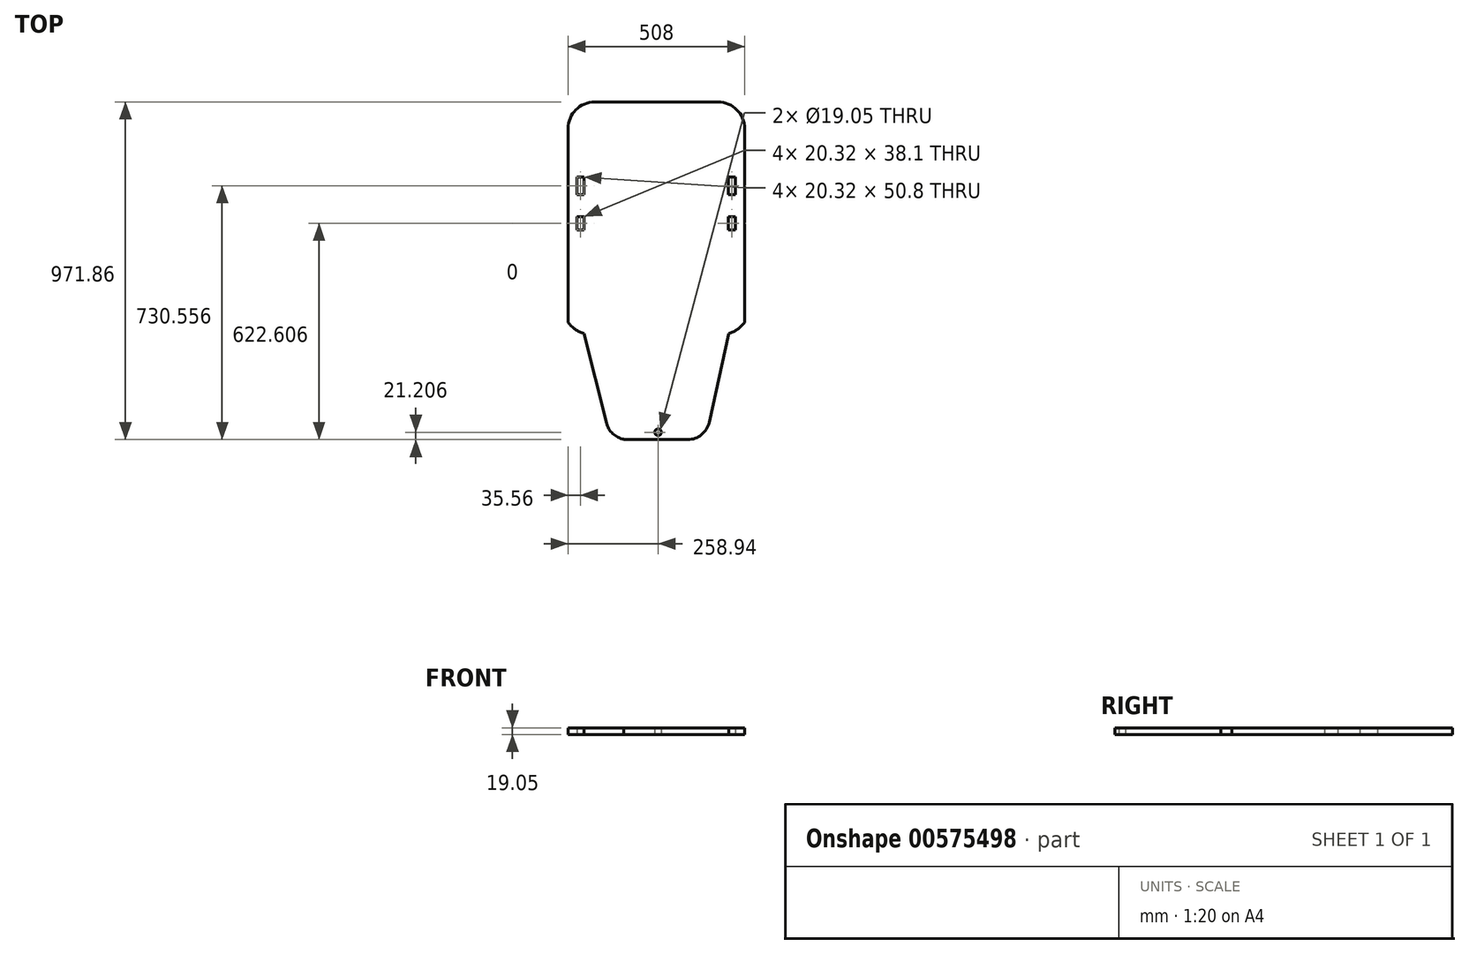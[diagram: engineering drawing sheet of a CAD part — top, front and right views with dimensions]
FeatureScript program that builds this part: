
annotation { "Feature Type Name" : "Feature", "Feature Type Description" : "" }
export const myFeature = defineFeature(function(context is Context, id is Id, definition is map)
    precondition{}
    {
        {
            var Q0;
            Q0=qCreatedBy(makeId("Top.planeOp"),FACE);
            var sketch = newSketch(context, id + "F0", { "sketchPlane" : qUnion([Q0])});
            skLineSegment(sketch, "E0.bottom", {"start": v(-318.66, 535.1) * mm, "end": v(189.34, 535.1) * mm});
            skLineSegment(sketch, "E0.left", {"start": v(-318.66, 535.1) * mm, "end": v(-318.66, 65.2) * mm});
            skLineSegment(sketch, "E0.right", {"start": v(189.34, 535.1) * mm, "end": v(189.34, 65.2) * mm});
            skLineSegment(sketch, "E1", {"start": v(87.68, -221.66) * mm, "end": v(143.12, 33.14) * mm});
            skLineSegment(sketch, "E2", {"start": v(-318.66, 535.1) * mm, "end": v(-242.46, 535.1) * mm});
            skLineSegment(sketch, "E3", {"start": v(189.34, 535.1) * mm, "end": v(113.14, 535.1) * mm});
            skLineSegment(sketch, "E4", {"start": v(-318.66, 535.1) * mm, "end": v(-318.66, 331.9) * mm});
            skLineSegment(sketch, "E5", {"start": v(189.34, 535.1) * mm, "end": v(189.34, 331.9) * mm});
            skLineSegment(sketch, "E6", {"start": v(-318.66, 331.9) * mm, "end": v(-293.26, 331.9) * mm});
            skLineSegment(sketch, "E7", {"start": v(-242.46, 535.1) * mm, "end": v(-242.46, 370) * mm});
            skLineSegment(sketch, "E8.top", {"start": v(-242.46, 331.9) * mm, "end": v(-293.26, 331.9) * mm});
            skLineSegment(sketch, "E8.left", {"start": v(-242.46, 370) * mm, "end": v(-242.46, 331.9) * mm});
            skLineSegment(sketch, "E8.right", {"start": v(-293.26, 370) * mm, "end": v(-293.26, 331.9) * mm});
            skLineSegment(sketch, "E9", {"start": v(113.14, 535.1) * mm, "end": v(113.14, 370) * mm});
            skLineSegment(sketch, "E10", {"start": v(189.34, 331.9) * mm, "end": v(163.94, 331.9) * mm});
            skLineSegment(sketch, "E11.top", {"start": v(113.14, 331.9) * mm, "end": v(163.94, 331.9) * mm});
            skLineSegment(sketch, "E11.left", {"start": v(113.14, 370) * mm, "end": v(113.14, 331.9) * mm});
            skLineSegment(sketch, "E12", {"start": v(-318.66, 535.1) * mm, "end": v(-64.66, 535.1) * mm});
            skPoint(sketch, "E13.endSnap0", {"position": v(-318.66, 433.5) * mm});
            skLineSegment(sketch, "E14", {"start": v(-293.26, 433.5) * mm, "end": v(-293.26, 484.3) * mm});
            skLineSegment(sketch, "E15.top", {"start": v(-242.46, 700.2) * mm, "end": v(113.14, 700.2) * mm});
            skLineSegment(sketch, "E15.left", {"start": v(-318.66, 535.1) * mm, "end": v(-318.66, 624) * mm});
            skLineSegment(sketch, "E15.right", {"start": v(189.34, 535.1) * mm, "end": v(189.34, 624) * mm});
            skLineSegment(sketch, "E16", {"start": v(-293.26, 370) * mm, "end": v(-272.94, 370) * mm});
            skLineSegment(sketch, "E17", {"start": v(-272.94, 370) * mm, "end": v(-272.94, 331.9) * mm});
            skLineSegment(sketch, "E18", {"start": v(-293.26, 433.5) * mm, "end": v(-272.94, 433.5) * mm});
            skLineSegment(sketch, "E19", {"start": v(-272.94, 433.5) * mm, "end": v(-272.94, 484.3) * mm});
            skLineSegment(sketch, "E20", {"start": v(-293.26, 484.3) * mm, "end": v(-272.94, 484.3) * mm});
            skLineSegment(sketch, "E21.MirrorCS", {"start": v(142.35, 433.5) * mm, "end": v(142.35, 484.3) * mm});
            skLineSegment(sketch, "E22.MirrorCS", {"start": v(162.67, 370) * mm, "end": v(162.67, 331.9) * mm});
            skLineSegment(sketch, "E23.MirrorCS", {"start": v(162.67, 484.3) * mm, "end": v(142.35, 484.3) * mm});
            skLineSegment(sketch, "E24.MirrorCS", {"start": v(162.67, 433.5) * mm, "end": v(162.67, 484.3) * mm});
            skLineSegment(sketch, "E25.MirrorCS", {"start": v(162.67, 370) * mm, "end": v(142.35, 370) * mm});
            skLineSegment(sketch, "E26.MirrorCS", {"start": v(142.35, 370) * mm, "end": v(142.35, 331.9) * mm});
            skLineSegment(sketch, "E27.MirrorCS", {"start": v(162.67, 433.5) * mm, "end": v(142.35, 433.5) * mm});
            skArc(sketch, "E28", {"start": v(-318.66, 65.2) * mm, "mid": v(-298.07, 45.54) * mm, "end": v(-272.44, 33.14) * mm});
            skLineSegment(sketch, "E29", {"start": v(-64.66, 535.1) * mm, "end": v(-64.66, 471.56) * mm});
            skArc(sketch, "E30.MirrorCS", {"start": v(189.34, 65.2) * mm, "mid": v(168.75, 45.54) * mm, "end": v(143.12, 33.14) * mm});
            skLineSegment(sketch, "E31", {"start": v(-272.44, 33.14) * mm, "end": v(-208.27, -223.56) * mm});
            skLineSegment(sketch, "E32", {"start": v(-146.67, -271.66) * mm, "end": v(25.64, -271.66) * mm});
            skLineSegment(sketch, "E33.top", {"start": v(-120.04, -271.66) * mm, "end": v(0.6, -271.66) * mm});
            skLineSegment(sketch, "E34.top", {"start": v(-120.04, -271.66) * mm, "end": v(-158.14, -271.66) * mm});
            skLineSegment(sketch, "E35.top", {"start": v(0.6, -271.66) * mm, "end": v(25.64, -271.66) * mm});
            skLineSegment(sketch, "E36", {"start": v(-158.14, -271.66) * mm, "end": v(-59.72, -271.66) * mm});
            skLineSegment(sketch, "E37", {"start": v(-59.72, -271.66) * mm, "end": v(-59.72, -250.45) * mm});
            skLineSegment(sketch, "E38", {"start": v(162.67, 433.5) * mm, "end": v(162.67, 370) * mm});
            skPoint(sketch, "E39.orphan", {"position": v(-158.14, -576.46) * mm});
            skPoint(sketch, "E40.end.orphan", {"position": v(-158.14, -297.06) * mm});
            skPoint(sketch, "E41.MirrorC.center.orphan", {"position": v(38.7, -297.06) * mm});
            skPoint(sketch, "E35.bottom.start.orphan", {"position": v(0.6, -322.46) * mm});
            skPoint(sketch, "E42.orphan", {"position": v(0.6, -271.66) * mm});
            skPoint(sketch, "E43.MirrorCS.start.orphan", {"position": v(76.8, -576.46) * mm});
            skPoint(sketch, "E44.MirrorCS.end.orphan", {"position": v(38.7, -576.46) * mm});
            skPoint(sketch, "E45.MirrorCS.start.orphan", {"position": v(0.6, -576.46) * mm});
            skPoint(sketch, "E46.orphan", {"position": v(0.6, -538.36) * mm});
            skPoint(sketch, "E47.end.orphan", {"position": v(-59.72, -576.46) * mm});
            skPoint(sketch, "E47.start.orphan", {"position": v(-59.72, -538.36) * mm});
            skPoint(sketch, "E48.left.end.orphan", {"position": v(-120.04, -538.36) * mm});
            skPoint(sketch, "E49.orphan", {"position": v(-120.04, -576.46) * mm});
            skPoint(sketch, "E34.bottom.end.orphan", {"position": v(-196.24, -576.46) * mm});
            skLineSegment(sketch, "E50", {"start": v(-158.14, -271.66) * mm, "end": v(-158.14, -246.26) * mm});
            skCircle(sketch, "E51", {"center": v(-59.72, -250.45) * mm, "radius": 9.53 * mm});
            skLineSegment(sketch, "E52", {"start": v(-59.72, -271.66) * mm, "end": v(-59.72, -304.7) * mm});
            skPoint(sketch, "E53.visualSharp", {"position": v(76.8, -271.66) * mm});
            skArc(sketch, "E53.filletArc", {"start": v(25.64, -271.66) * mm, "mid": v(65.48, -257.6) * mm, "end": v(87.68, -221.66) * mm});
            skPoint(sketch, "E54.visualSharp", {"position": v(-196.24, -271.66) * mm});
            skArc(sketch, "E54.filletArc", {"start": v(-208.27, -223.56) * mm, "mid": v(-185.74, -258.21) * mm, "end": v(-146.67, -271.66) * mm});
            skPoint(sketch, "E55.visualSharp", {"position": v(-318.66, 700.2) * mm});
            skArc(sketch, "E55.filletArc", {"start": v(-242.46, 700.2) * mm, "mid": v(-296.34, 677.88) * mm, "end": v(-318.66, 624) * mm});
            skPoint(sketch, "E56.visualSharp", {"position": v(189.34, 700.2) * mm});
            skArc(sketch, "E56.filletArc", {"start": v(189.34, 624) * mm, "mid": v(167.02, 677.88) * mm, "end": v(113.14, 700.2) * mm});
            skSolve(sketch);
        }
        {
            var Q0;
            Q0=makeQuery(id+"F0.imprint","IMPRINT",FACE,{"disambiguationData":[TD([[makeQuery(id+"F0.imprint","IMPRINT",EDGE,{"derivedFrom":sQuery(id+"F0.wireOp",EDGE,"E0.bottom")}),-1.0]])]});
            var Q1;
            Q1=makeQuery(id+"F0.imprint","IMPRINT",FACE,{"disambiguationData":[TD([[makeQuery(id+"F0.imprint","IMPRINT",EDGE,{"derivedFrom":sQuery(id+"F0.wireOp",EDGE,"E2")}),-1.0]])]});
            var Q2;
            Q2=makeQuery(id+"F0.imprint","IMPRINT",FACE,{"disambiguationData":[TD([[makeQuery(id+"F0.imprint","IMPRINT",EDGE,{"derivedFrom":sQuery(id+"F0.wireOp",EDGE,"E3")}),1.0]])]});
            extrude(context, id + "F1", {"entities" : qUnion([Q0, Q1, Q2]), "depth" : 19.05 * mm, "offsetDistance" : 25.4 * mm});
        }
        {
            var Q0;
            Q0 = qSketchRegion(id + "F0", true);
            extrude(context, id + "F2", {"entities" : qUnion([Q0]), "operationType" : NewBodyOperationType.ADD, "depth" : 19.05 * mm, "offsetDistance" : 25.4 * mm});
        }
        {
            var Q0;
            Q0 = qSketchRegion(id + "F0", true);
            extrude(context, id + "F3", {"entities" : qUnion([Q0]), "depth" : 19.05 * mm, "offsetDistance" : 25.4 * mm});
        }
    });
